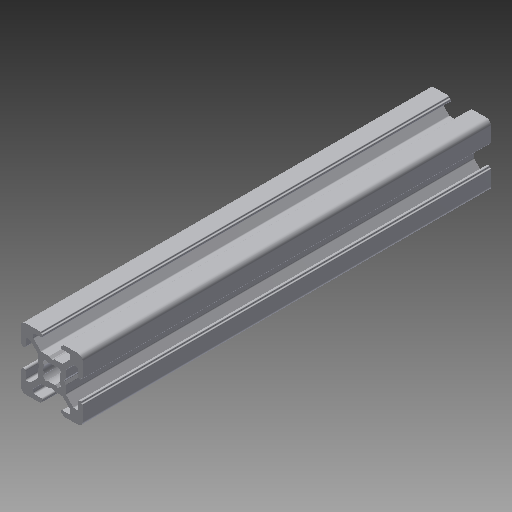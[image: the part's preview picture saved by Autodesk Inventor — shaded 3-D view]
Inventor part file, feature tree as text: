
AUTODESK INVENTOR PART (.ipt)
format: ipt  version: 2017 (Build 210142000, 142)  size: 320,512 bytes
history: native  units: in
note: dims shown in document units (in); Inventor stores cm internally (conversion verified against a paired STEP export)
features: other x3, extrude x1, sketch x1
ambient origin geometry x8: Origin, YZ Plane, XZ Plane, XY Plane, X Axis, Y Axis, Z Axis, Center Point
bodies: Solid1 (feature_tree)
feature tree (5):
  other  "Blocks"
  extrude  "Extrusion1"  [1 undecoded]
  sketch  "Sketch1"  dims[d1=0.0in]
  other  "20x20"
  other  "20x20:1"
note: 1 required parameter value undecoded (feature->parameter linkage not recoverable at this tier; creation-order binding heuristic only, values carry confidence <= 0.55)
